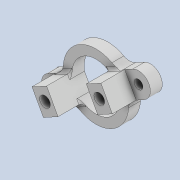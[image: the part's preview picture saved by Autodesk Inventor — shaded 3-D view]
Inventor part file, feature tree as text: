
AUTODESK INVENTOR PART (.ipt)
format: ipt  version: 2020 (Build 240168000, 168)  size: 215,040 bytes
history: native  units: mm
features: other x5, extrude x4, sketch x3, fillet x2, reference x2, projected_geometry x2, plane x1
ambient origin geometry x8: Origin, YZ Plane, XZ Plane, XY Plane, X Axis, Y Axis, Z Axis, Center Point
bodies: Solid1 (feature_tree)
feature tree (19):
  extrude  "Extrusion1"  Depth=8.0mm
  extrude  "Extrusion3"  Depth=2.0mm TaperAngle=0.0deg
  sketch  "Sketch5"  dims[d7=5.2mm d8=5.2mm d9=1.8mm d10=1.8mm d11=2.0mm d12=0.0mm d13=4.0mm d14=2.8mm d15=4.0mm d16=2.8mm d17=2.0mm d18=0.0mm d19=4.0mm d20=0.0mm d21=2.0mm d25=0.5mm]
  extrude  "Extrusion4"  Depth=0.5mm
  plane  "Work Plane1"
  extrude  "Extrusion5"  Depth=0.5mm
  fillet  "Fillet1"  Radius=1.8mm
  fillet  "Fillet2"  Radius=2.0mm
  sketch  "Sketch1"  dims[d0=4.0mm d1=8.0mm]
  reference  "Reference1"
  reference  "Reference2"
  sketch  "Sketch4"  dims[d2=11.0mm d3=2.0mm d4=0.0mm]
  projected_geometry  "Projected Loop2"
  projected_geometry  "Projected Loop3"
  parser-record x1  (decoder bookkeeping rows leaked as tree rows — omitted from the tree; the rows remain in map.json)
  other  "tip_ass_t1.iam"
  other  "pin_conn_1:1"
  other  "motor_1608:1"
  other  "motor_1608_inner:1"
note: 1 file-system path scrubbed to <path> (originals preserved in map.json)
